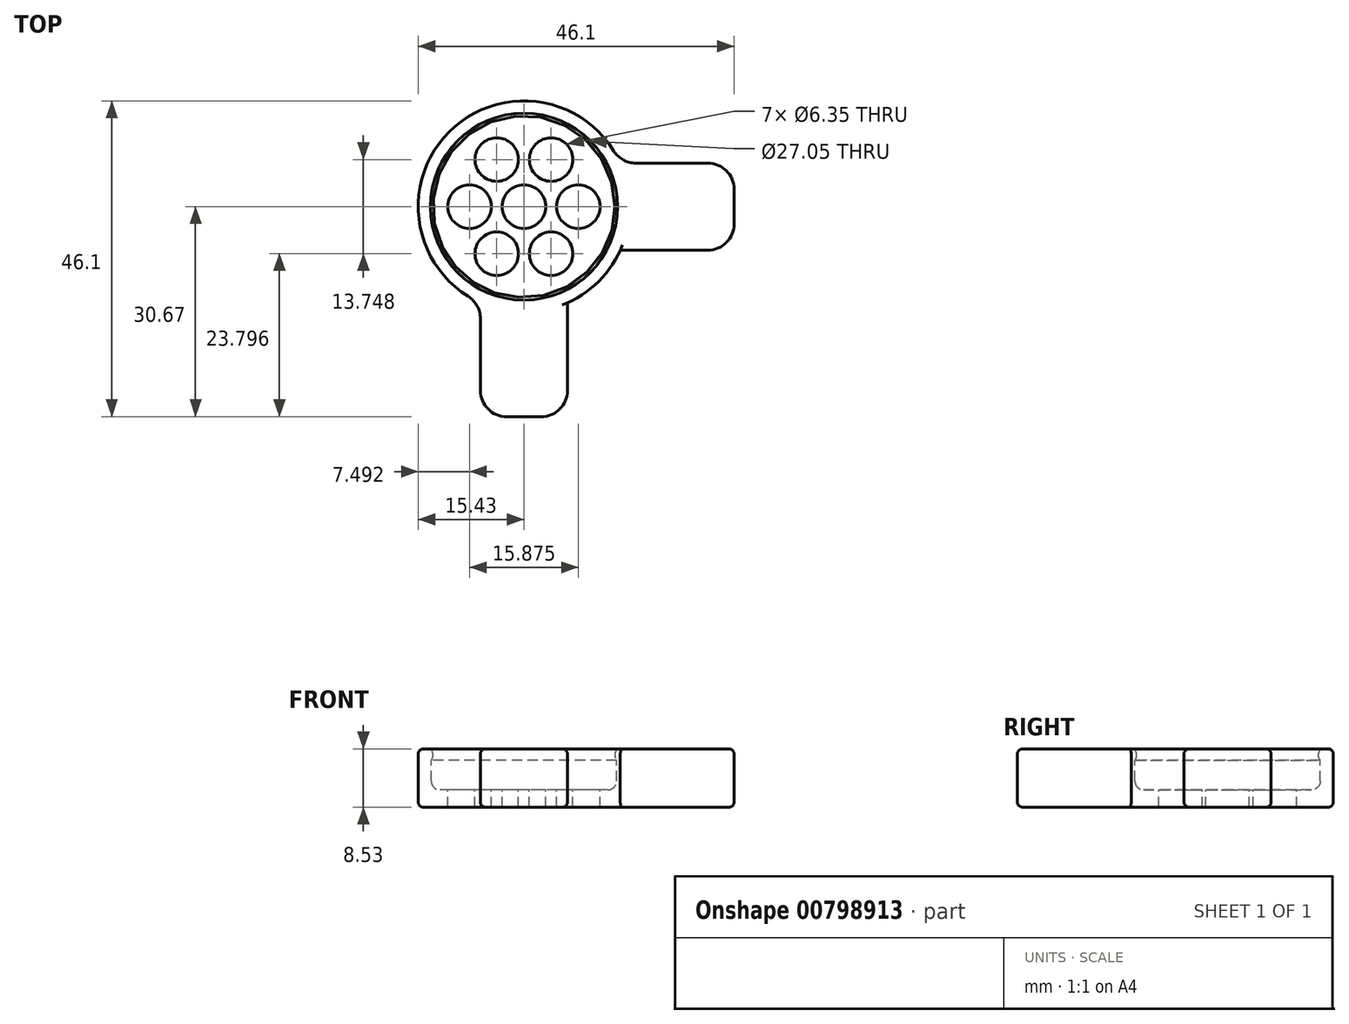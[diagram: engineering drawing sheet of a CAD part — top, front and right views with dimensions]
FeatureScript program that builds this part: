
annotation { "Feature Type Name" : "Feature", "Feature Type Description" : "" }
export const myFeature = defineFeature(function(context is Context, id is Id, definition is map)
    precondition{}
    {
        {
            var Q0;
            Q0=qCreatedBy(makeId("Front.planeOp"),FACE);
            var sketch = newSketch(context, id + "F0", { "sketchPlane" : qUnion([Q0])});
            skLineSegment(sketch, "E0", {"start": v(15.43, 6.71) * mm, "end": v(15.43, 0) * mm});
            skLineSegment(sketch, "E1", {"start": v(15.43, 0) * mm, "end": v(0, 0) * mm});
            skArc(sketch, "E2", {"start": v(15.43, 6.71) * mm, "mid": v(13.63, 6.73) * mm, "end": v(13.65, 8.53) * mm});
            skLineSegment(sketch, "E3", {"start": v(0, 10.9) * mm, "end": v(0, -2.45) * mm, "construction": true});
            skLineSegment(sketch, "E4", {"start": v(0, 0) * mm, "end": v(0, 2.54) * mm});
            skLineSegment(sketch, "E5", {"start": v(0, 2.54) * mm, "end": v(12.26, 2.54) * mm});
            skLineSegment(sketch, "E6", {"start": v(13.53, 3.81) * mm, "end": v(13.53, 6.86) * mm});
            skLineSegment(sketch, "E7", {"start": v(15.43, 6.71) * mm, "end": v(15.43, 8.53) * mm});
            skLineSegment(sketch, "E8", {"start": v(15.43, 8.53) * mm, "end": v(13.65, 8.53) * mm});
            skPoint(sketch, "E9.visualSharp", {"position": v(13.53, 2.54) * mm});
            skArc(sketch, "E10.filletArc", {"start": v(12.26, 2.54) * mm, "mid": v(13.15, 2.91) * mm, "end": v(13.53, 3.81) * mm});
            skPoint(sketch, "E11.visualSharp", {"position": v(15.43, 0) * mm});
            skPoint(sketch, "E12.visualSharp", {"position": v(15.43, 8.53) * mm});
            skSolve(sketch);
        }
        {
            var Q0;
            Q0=qSketchRegion(id+"F0",true);
            var Q1;
            Q1=sQuery(id+"F0.wireOp",EDGE,"E3");
            revolve(context, id + "F1", {"surfaceOperationType" : NewSurfaceOperationType.NEW, "entities" : qUnion([Q0]), "axis" : qUnion([Q1]), "revolveType" : RevolveType.FULL});
        }
        {
            var Q0;
            Q0=makeQuery(id+"F1.opRevolve","SWEPT_FACE",FACE,{"disambiguationData":[OSD([sQuery(id+"F0.wireOp",EDGE,"E8")])]});
            var sketch = newSketch(context, id + "F2", { "sketchPlane" : qUnion([Q0])});
            skLineSegment(sketch, "E13.bottom", {"start": v(30.67, 6.35) * mm, "end": v(14.06, 6.35) * mm});
            skLineSegment(sketch, "E13.top", {"start": v(30.67, -6.35) * mm, "end": v(14.06, -6.35) * mm});
            skLineSegment(sketch, "E13.left", {"start": v(30.67, 6.35) * mm, "end": v(30.67, -6.35) * mm});
            skLineSegment(sketch, "E14.bottom", {"start": v(6.35, -30.67) * mm, "end": v(-6.35, -30.67) * mm});
            skLineSegment(sketch, "E14.left", {"start": v(6.35, -30.67) * mm, "end": v(6.35, -14.06) * mm});
            skLineSegment(sketch, "E14.right", {"start": v(-6.35, -30.67) * mm, "end": v(-6.35, -14.06) * mm});
            skArc(sketch, "E15.0", {"start": v(-6.35, -14.06) * mm, "mid": v(0, -15.43) * mm, "end": v(6.35, -14.06) * mm});
            skArc(sketch, "E16.trimOffspring", {"start": v(14.06, -6.35) * mm, "mid": v(15.43, 0) * mm, "end": v(14.06, 6.35) * mm});
            skSolve(sketch);
        }
        {
            var Q0;
            Q0=qSketchRegion(id+"F2",true);
            var Q1;
            Q1=makeQuery(id+"F1.opRevolve","SWEPT_FACE",FACE,{"disambiguationData":[OSD([sQuery(id+"F0.wireOp",EDGE,"E1")])]});
            extrude(context, id + "F3", {"entities" : qUnion([Q0]), "operationType" : NewBodyOperationType.ADD, "endBound" : BoundingType.UP_TO_SURFACE, "oppositeDirection" : true, "depth" : 25.4 * mm, "endBoundEntityFace" : qUnion([Q1]), "offsetDistance" : 25.4 * mm});
        }
        {
            var Q0;
            Q0=makeQuery(id+"F3.opExtrude","SWEPT_EDGE",EDGE,{"disambiguationData":[OSD([sQuery(id+"F2.wireOp",EDGE,"E14.bottom"),sQuery(id+"F2.wireOp",EDGE,"E14.right")])]});
            var Q1;
            Q1=makeQuery(id+"F3.opExtrude","SWEPT_EDGE",EDGE,{"disambiguationData":[OSD([sQuery(id+"F0.wireOp",EDGE,"E7"),sQuery(id+"F0.wireOp",EDGE,"E8"),sQuery(id+"F2.wireOp",EDGE,"E14.right"),sQuery(id+"F2.wireOp",EDGE,"E15.0")])]});
            var Q2;
            Q2=makeQuery(id+"F3.opExtrude","SWEPT_EDGE",EDGE,{"disambiguationData":[OSD([sQuery(id+"F2.wireOp",EDGE,"E14.bottom"),sQuery(id+"F2.wireOp",EDGE,"E14.left")])]});
            var Q3;
            Q3=makeQuery(id+"F3.opExtrude","SWEPT_EDGE",EDGE,{"disambiguationData":[OSD([sQuery(id+"F0.wireOp",EDGE,"E7"),sQuery(id+"F0.wireOp",EDGE,"E8"),sQuery(id+"F2.wireOp",EDGE,"E14.left"),sQuery(id+"F2.wireOp",EDGE,"E15.0")])]});
            var Q4;
            Q4=makeQuery(id+"F3.opExtrude","SWEPT_EDGE",EDGE,{"disambiguationData":[OSD([sQuery(id+"F0.wireOp",EDGE,"E7"),sQuery(id+"F0.wireOp",EDGE,"E8"),sQuery(id+"F2.wireOp",EDGE,"E13.top"),sQuery(id+"F2.wireOp",EDGE,"E16.trimOffspring")])]});
            var Q5;
            Q5=makeQuery(id+"F3.opExtrude","SWEPT_EDGE",EDGE,{"disambiguationData":[OSD([sQuery(id+"F2.wireOp",EDGE,"E13.top"),sQuery(id+"F2.wireOp",EDGE,"E13.left")])]});
            var Q6;
            Q6=makeQuery(id+"F3.opExtrude","SWEPT_EDGE",EDGE,{"disambiguationData":[OSD([sQuery(id+"F2.wireOp",EDGE,"E13.bottom"),sQuery(id+"F2.wireOp",EDGE,"E13.left")])]});
            var Q7;
            Q7=makeQuery(id+"F3.opExtrude","SWEPT_EDGE",EDGE,{"disambiguationData":[OSD([sQuery(id+"F0.wireOp",EDGE,"E7"),sQuery(id+"F0.wireOp",EDGE,"E8"),sQuery(id+"F2.wireOp",EDGE,"E13.bottom"),sQuery(id+"F2.wireOp",EDGE,"E16.trimOffspring")])]});
            fillet(context, id + "F4", {"entities" : qUnion([Q0, Q1, Q2, Q3, Q4, Q5, Q6, Q7]), "radius" : 3.8 * mm, "tangentPropagation" : true, "allowEdgeOverflow" : false});
        }
        {
            var Q0;
            Q0=makeQuery(id+"F3.opExtrude","CAP_EDGE",EDGE,{"disambiguationData":[OSD([sQuery(id+"F2.wireOp",EDGE,"E14.bottom")])],"isStart":true});
            var Q1;
            Q1=makeQuery(id+"F3.opExtrude","CAP_EDGE",EDGE,{"disambiguationData":[OSD([sQuery(id+"F2.wireOp",EDGE,"E14.bottom")])],"isStart":false});
            fillet(context, id + "F5", {"entities" : qUnion([Q0, Q1]), "radius" : 0.76 * mm, "tangentPropagation" : true, "allowEdgeOverflow" : false});
        }
        {
            var Q0;
            Q0=makeQuery(id+"F1.opRevolve","SWEPT_FACE",FACE,{"disambiguationData":[OSD([sQuery(id+"F0.wireOp",EDGE,"E5")])]});
            var sketch = newSketch(context, id + "F6", { "sketchPlane" : qUnion([Q0])});
            skCircle(sketch, "E17", {"center": v(-6.7, 7.93) * mm, "radius": 1.4 * mm});
            skCircle(sketch, "E18.1.0.0", {"center": v(-2.25, 7.93) * mm, "radius": 1.4 * mm});
            skCircle(sketch, "E18.2.0.0", {"center": v(2.2, 7.93) * mm, "radius": 1.4 * mm});
            skCircle(sketch, "E18.3.0.0", {"center": v(6.64, 7.93) * mm, "radius": 1.4 * mm});
            skLineSegment(sketch, "E18.direction1", {"start": v(-6.7, 7.93) * mm, "end": v(-2.25, 7.93) * mm, "construction": true});
            skCircle(sketch, "E19", {"center": v(-8.66, 4.6) * mm, "radius": 1.4 * mm});
            skCircle(sketch, "E20.1.0.0", {"center": v(-4.22, 4.6) * mm, "radius": 1.4 * mm});
            skCircle(sketch, "E20.2.0.0", {"center": v(0.23, 4.6) * mm, "radius": 1.4 * mm});
            skCircle(sketch, "E20.3.0.0", {"center": v(4.67, 4.6) * mm, "radius": 1.4 * mm});
            skLineSegment(sketch, "E20.direction1", {"start": v(-8.66, 4.6) * mm, "end": v(-4.22, 4.6) * mm, "construction": true});
            skCircle(sketch, "E21.3.0.0", {"center": v(8.32, 4.74) * mm, "radius": 1.34 * mm});
            skCircle(sketch, "E22", {"center": v(-6.88, 1.46) * mm, "radius": 1.4 * mm});
            skCircle(sketch, "E23.1.0.0", {"center": v(-2.44, 1.46) * mm, "radius": 1.4 * mm});
            skCircle(sketch, "E23.2.0.0", {"center": v(2, 1.46) * mm, "radius": 1.4 * mm});
            skCircle(sketch, "E23.3.0.0", {"center": v(6.45, 1.46) * mm, "radius": 1.4 * mm});
            skLineSegment(sketch, "E23.direction1", {"start": v(-6.88, 1.46) * mm, "end": v(-2.44, 1.46) * mm, "construction": true});
            skCircle(sketch, "E24", {"center": v(-8.85, -1.87) * mm, "radius": 1.4 * mm});
            skCircle(sketch, "E25.1.0.0", {"center": v(-4.4, -1.87) * mm, "radius": 1.4 * mm});
            skCircle(sketch, "E25.2.0.0", {"center": v(0.04, -1.87) * mm, "radius": 1.4 * mm});
            skCircle(sketch, "E25.3.0.0", {"center": v(4.49, -1.87) * mm, "radius": 1.4 * mm});
            skLineSegment(sketch, "E25.direction1", {"start": v(-8.85, -1.87) * mm, "end": v(-4.4, -1.87) * mm, "construction": true});
            skCircle(sketch, "E26.3.0.0", {"center": v(8.13, -1.73) * mm, "radius": 1.34 * mm});
            skCircle(sketch, "E27", {"center": v(-6.6, -4.9) * mm, "radius": 1.4 * mm});
            skCircle(sketch, "E28.1.0.0", {"center": v(-2.16, -4.9) * mm, "radius": 1.4 * mm});
            skCircle(sketch, "E28.2.0.0", {"center": v(2.29, -4.9) * mm, "radius": 1.4 * mm});
            skCircle(sketch, "E28.3.0.0", {"center": v(6.73, -4.9) * mm, "radius": 1.4 * mm});
            skLineSegment(sketch, "E28.direction1", {"start": v(-6.6, -4.9) * mm, "end": v(-2.16, -4.9) * mm, "construction": true});
            skCircle(sketch, "E29", {"center": v(-4.25, -8.22) * mm, "radius": 1.4 * mm});
            skCircle(sketch, "E30.1.0.0", {"center": v(0.2, -8.22) * mm, "radius": 1.4 * mm});
            skCircle(sketch, "E30.2.0.0", {"center": v(4.64, -8.22) * mm, "radius": 1.4 * mm});
            skLineSegment(sketch, "E30.direction1", {"start": v(-4.25, -8.22) * mm, "end": v(0.2, -8.22) * mm, "construction": true});
            skSolve(sketch);
        }
        {
            var Q0;
            Q0=makeQuery(id+"F6.imprint","IMPRINT",FACE,{"disambiguationData":[TD([[makeQuery(id+"F6.imprint","IMPRINT",EDGE,{"derivedFrom":sQuery(id+"F6.wireOp",EDGE,"E17")}),-1.0]])]});
            var sketch = newSketch(context, id + "F7", { "sketchPlane" : qUnion([Q0])});
            skCircle(sketch, "E31", {"center": v(-3.97, 6.87) * mm, "radius": 3.18 * mm});
            skCircle(sketch, "E32", {"center": v(0, 0) * mm, "radius": 3.18 * mm});
            skLineSegment(sketch, "E33", {"start": v(-3.97, 6.87) * mm, "end": v(0, 0) * mm, "construction": true});
            skLineSegment(sketch, "E34", {"start": v(0, 0) * mm, "end": v(-19.87, 0) * mm, "construction": true});
            skCircle(sketch, "E35.1.0", {"center": v(-7.94, 0) * mm, "radius": 3.18 * mm});
            skCircle(sketch, "E35.2.0", {"center": v(-3.97, -6.87) * mm, "radius": 3.18 * mm});
            skCircle(sketch, "E35.3.0", {"center": v(3.97, -6.87) * mm, "radius": 3.18 * mm});
            skCircle(sketch, "E35.4.0", {"center": v(7.94, 0) * mm, "radius": 3.18 * mm});
            skCircle(sketch, "E35.5.0", {"center": v(3.97, 6.87) * mm, "radius": 3.18 * mm});
            skSolve(sketch);
        }
        {
            var Q0;
            Q0 = qSketchRegion(id + "F7", true);
            extrude(context, id + "F8", {"entities" : qUnion([Q0]), "operationType" : NewBodyOperationType.REMOVE, "oppositeDirection" : true, "depth" : 25.4 * mm, "offsetDistance" : 25.4 * mm});
        }
    });
